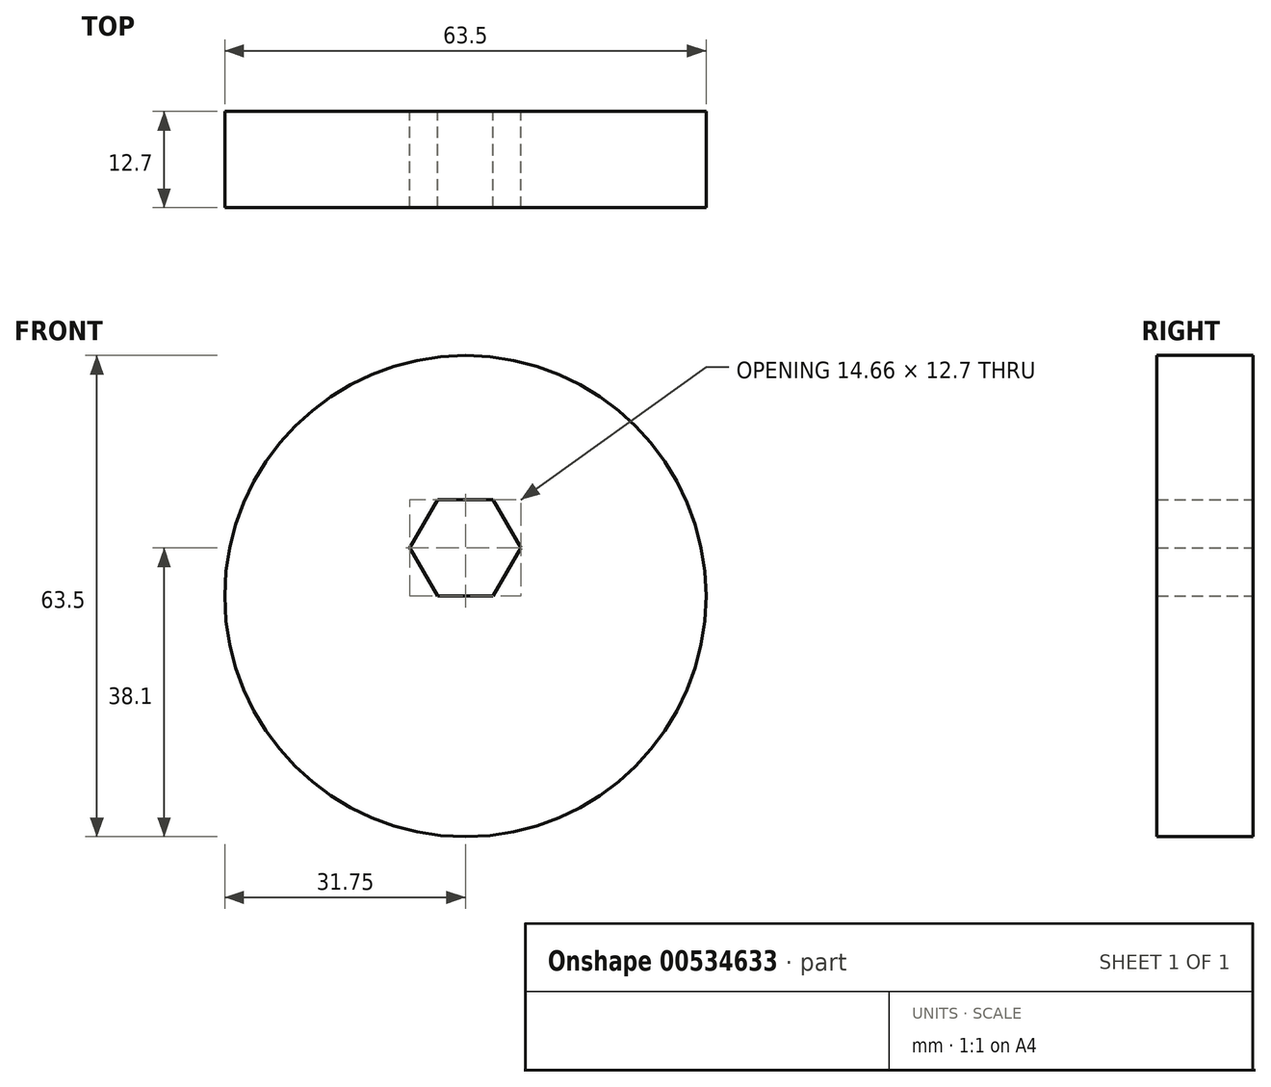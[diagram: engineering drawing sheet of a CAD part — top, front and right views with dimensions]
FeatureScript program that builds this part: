
annotation { "Feature Type Name" : "Feature", "Feature Type Description" : "" }
export const myFeature = defineFeature(function(context is Context, id is Id, definition is map)
    precondition{}
    {
        {
            var Q0;
            Q0=qCreatedBy(makeId("Front.planeOp"),FACE);
            var sketch = newSketch(context, id + "F0", { "sketchPlane" : qUnion([Q0])});
            skCircle(sketch, "E0.cCircle", {"center": v(0, 0) * mm, "radius": 6.35 * mm, "construction": true});
            skLineSegment(sketch, "E0.0", {"start": v(-7.33, 0) * mm, "end": v(-3.67, 6.35) * mm});
            skLineSegment(sketch, "E0.1", {"start": v(-3.67, 6.35) * mm, "end": v(3.67, 6.35) * mm});
            skLineSegment(sketch, "E0.2", {"start": v(3.67, 6.35) * mm, "end": v(7.33, 0) * mm});
            skLineSegment(sketch, "E0.3", {"start": v(7.33, 0) * mm, "end": v(3.67, -6.35) * mm});
            skLineSegment(sketch, "E0.4", {"start": v(3.67, -6.35) * mm, "end": v(-3.67, -6.35) * mm});
            skLineSegment(sketch, "E0.5", {"start": v(-3.67, -6.35) * mm, "end": v(-7.33, 0) * mm});
            skPoint(sketch, "E0.0.midPoint", {"position": v(-5.5, 3.18) * mm});
            skCircle(sketch, "E1", {"center": v(0, -6.35) * mm, "radius": 31.75 * mm});
            skPoint(sketch, "E1.centerSnap0", {"position": v(0, 6.35) * mm});
            skSolve(sketch);
        }
        {
            var Q0;
            Q0=makeQuery(id+"F0.imprint","IMPRINT",FACE,{"disambiguationData":[TD([[makeQuery(id+"F0.imprint","IMPRINT",EDGE,{"derivedFrom":sQuery(id+"F0.wireOp",EDGE,"E0.0")}),1.0]])]});
            extrude(context, id + "F1", {"entities" : qUnion([Q0]), "depth" : 12.7 * mm, "offsetDistance" : 25.4 * mm});
        }
    });
